# Revit family: Quiet-SqrTop_SqrBase
name_source: partatom
category: Furniture
revit_build: Autodesk Revit 2016 (Build: 20150714_1515(x64)
units: mm (PartAtom-declared; Revit-internal decimal feet)

## family parameters
Always vertical = Yes
Cut with Voids When Loaded = No
OmniClass Number = 23.40.20.14.14.17
OmniClass Title = Stools
Room Calculation Point = No
Shared = No
Work Plane-Based = No

## types (15) — shared parameters
Manufacturer = Bernhardt Design
URL = http://bernhardtdesign.com

## per-type parameters (varying)
| type | Base Width | Catalog | Column Radius | Depth | Height | SKU | Width |
| Quiet - QUS-184 18" sqr top/ sqr base occasional | 12" | QUS-184 | 3/8" | 18" | 18" | QUS-184 | 18" |
| Quiet - QUS-224 22" sqr top/ sqr base occasional | 16" | QUS-224 | 3/8" | 22" | 18" | QUS-224 | 22" |
| Quiet - QUS-304 30" sqr top/ sqr base occasional | 17 3/4" | QUS-304 | 1 1/2" | 30" | 13" | QUS-304 | 30" |
| Quiet - QUS-364 36" sqr top/ sqr base occasional | 17 3/4" | QUS-364 | 1 1/2" | 36" | 13" | QUS-364 | 36" |
| Quiet - QUS-424 42" sqr top/ sqr base occasional | 21 5/8" | QUS-424 | 1 1/2" | 42" | 13" | QUS-424 | 42" |
| Quiet - QUS-188 18" sqr top/ sqr base mid | 12" | QUS-188 | 7/16" | 18" | 23 3/4" | QUS-188 | 18" |
| Quiet - QUS-228 22" sqr top/ sqr base mid | 16" | QUS-228 | 7/16" | 22" | 23 3/4" | QUS-228 | 22" |
| Quiet - QUS-308 30" sqr top/ sqr base mid | 17 3/4" | QUS-308 | 1 1/2" | 30" | 23 3/4" | QUS-308 | 30" |
| Quiet - QUS-368 36" sqr top/ sqr base mid | 17 3/4" | QUS-368 | 1 1/2" | 36" | 23 3/4" | QUS-368 | 36" |
| Quiet - QUS-428 42" sqr top/ sqr base mid | 21 5/8" | QUS-428 | 1 1/2" | 42" | 23 3/4" | QUS-428 | 42" |
| Quiet - QUS-312 30" sqr top/ sqr base conference | 17 3/4" | QUS-312 | 1 1/2" | 30" | 29" | QUS-312 | 30" |
| Quiet - QUS-372 36" sqr top/ sqr base conference | 17 3/4" | QUS-372 | 1 1/2" | 36" | 29" | QUS-372 | 36" |
| Quiet - QUS-432 42" sqr top/ sqr base conference | 21 5/8" | QUS-432 | 1 1/2" | 42" | 29" | QUS-432 | 42" |
| Quiet - QUS-274 27" sqr top/ sqr base bar | 17 3/4" | QUS-274 | 1 1/2" | 27" | 42" | QUS-274 | 27" |
| Quiet - QUS-316 30" sqr top/ sqr base bar | 17 3/4" | QUS-316 | 1 1/2" | 30" | 42" | QUS-316 | 30" |

## geometry (parser evidence)
native form markers: Blend x2, Sweep x2
no freeform markers — native parametric forms only
